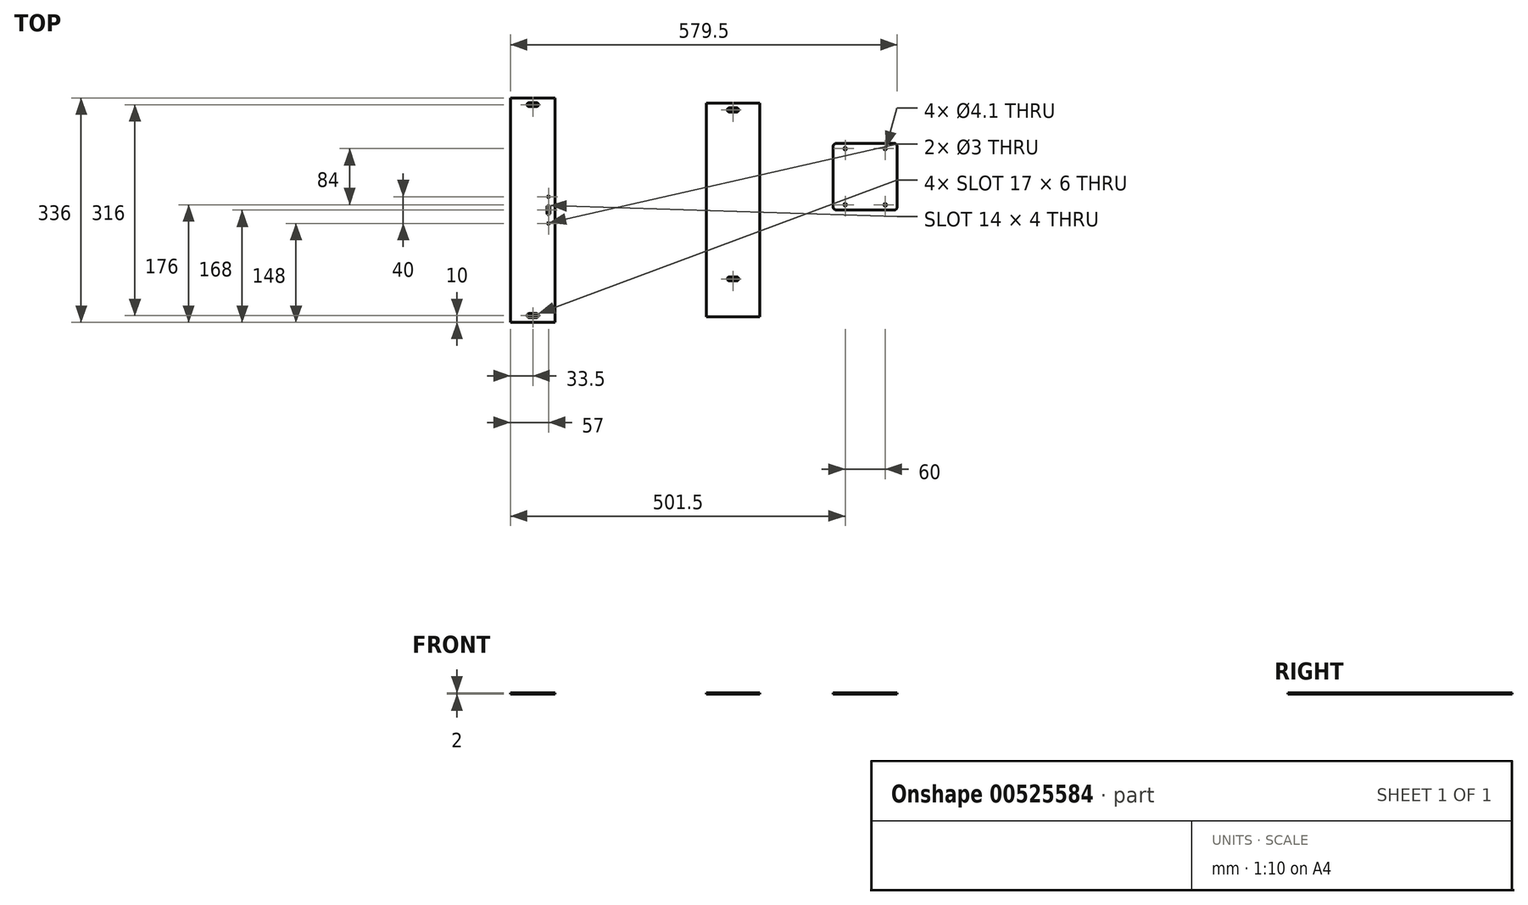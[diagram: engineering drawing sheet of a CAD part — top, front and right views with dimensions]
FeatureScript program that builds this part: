
annotation { "Feature Type Name" : "Feature", "Feature Type Description" : "" }
export const myFeature = defineFeature(function(context is Context, id is Id, definition is map)
    precondition{}
    {
        {
            var Q0;
            Q0=qCreatedBy(makeId("Top.planeOp"),FACE);
            var sketch = newSketch(context, id + "F0", { "sketchPlane" : qUnion([Q0])});
            skLineSegment(sketch, "E0.bottom", {"start": v(40, -160) * mm, "end": v(-40, -160) * mm});
            skLineSegment(sketch, "E0.top", {"start": v(40, 160) * mm, "end": v(-40, 160) * mm});
            skLineSegment(sketch, "E0.left", {"start": v(40, -160) * mm, "end": v(40, 160) * mm});
            skLineSegment(sketch, "E0.right", {"start": v(-40, -160) * mm, "end": v(-40, 160) * mm});
            skPoint(sketch, "E0.middle", {"position": v(0, 0) * mm});
            skLineSegment(sketch, "E1", {"start": v(-186.14, -93) * mm, "end": v(125.12, -93) * mm, "construction": true});
            skLineSegment(sketch, "E2", {"start": v(-183, -113) * mm, "end": v(135.04, -113) * mm, "construction": true});
            skLineSegment(sketch, "E3.bottom", {"start": v(5.5, -106) * mm, "end": v(-5.5, -106) * mm});
            skLineSegment(sketch, "E3.top", {"start": v(5.5, -100) * mm, "end": v(-5.5, -100) * mm});
            skLineSegment(sketch, "E3.left", {"start": v(5.5, -106) * mm, "end": v(5.5, -100) * mm, "construction": true});
            skLineSegment(sketch, "E3.right", {"start": v(-5.5, -106) * mm, "end": v(-5.5, -100) * mm, "construction": true});
            skPoint(sketch, "E3.middle", {"position": v(0, -103) * mm});
            skArc(sketch, "E4", {"start": v(5.5, -106) * mm, "mid": v(8.5, -103) * mm, "end": v(5.5, -100) * mm});
            skArc(sketch, "E5", {"start": v(-5.5, -100) * mm, "mid": v(-8.5, -103) * mm, "end": v(-5.5, -106) * mm});
            skLineSegment(sketch, "E6.bottom", {"start": v(5.5, 147) * mm, "end": v(-5.5, 147) * mm});
            skLineSegment(sketch, "E6.top", {"start": v(5.5, 153) * mm, "end": v(-5.5, 153) * mm});
            skLineSegment(sketch, "E6.left", {"start": v(5.5, 147) * mm, "end": v(5.5, 153) * mm, "construction": true});
            skLineSegment(sketch, "E6.right", {"start": v(-5.5, 147) * mm, "end": v(-5.5, 153) * mm, "construction": true});
            skPoint(sketch, "E6.middle", {"position": v(0, 150) * mm});
            skArc(sketch, "E7", {"start": v(5.5, 147) * mm, "mid": v(8.5, 150) * mm, "end": v(5.5, 153) * mm});
            skArc(sketch, "E8", {"start": v(-5.5, 153) * mm, "mid": v(-8.5, 150) * mm, "end": v(-5.5, 147) * mm});
            skLineSegment(sketch, "E9.bottom", {"start": v(-266.5, -168) * mm, "end": v(-333.5, -168) * mm});
            skLineSegment(sketch, "E9.top", {"start": v(-266.5, 168) * mm, "end": v(-333.5, 168) * mm});
            skLineSegment(sketch, "E9.left", {"start": v(-266.5, -168) * mm, "end": v(-266.5, 168) * mm});
            skLineSegment(sketch, "E9.right", {"start": v(-333.5, -168) * mm, "end": v(-333.5, 168) * mm});
            skPoint(sketch, "E9.middle", {"position": v(-300, 0) * mm});
            skLineSegment(sketch, "E10.bottom", {"start": v(-294.5, 155) * mm, "end": v(-305.5, 155) * mm});
            skLineSegment(sketch, "E10.top", {"start": v(-294.5, 161) * mm, "end": v(-305.5, 161) * mm});
            skLineSegment(sketch, "E10.left", {"start": v(-294.5, 155) * mm, "end": v(-294.5, 161) * mm, "construction": true});
            skLineSegment(sketch, "E10.right", {"start": v(-305.5, 155) * mm, "end": v(-305.5, 161) * mm, "construction": true});
            skPoint(sketch, "E10.middle", {"position": v(-300, 158) * mm});
            skArc(sketch, "E11", {"start": v(-294.5, 155) * mm, "mid": v(-291.5, 158) * mm, "end": v(-294.5, 161) * mm});
            skArc(sketch, "E12", {"start": v(-305.5, 161) * mm, "mid": v(-308.5, 158) * mm, "end": v(-305.5, 155) * mm});
            skLineSegment(sketch, "E13.MirrorCS", {"start": v(-305.5, -155) * mm, "end": v(-305.5, -161) * mm, "construction": true});
            skLineSegment(sketch, "E14.MirrorCS", {"start": v(-294.5, -155) * mm, "end": v(-294.5, -161) * mm, "construction": true});
            skLineSegment(sketch, "E15.MirrorCS", {"start": v(-294.5, -161) * mm, "end": v(-305.5, -161) * mm});
            skArc(sketch, "E16.MirrorCS", {"start": v(-294.5, -155) * mm, "mid": v(-291.5, -158) * mm, "end": v(-294.5, -161) * mm});
            skLineSegment(sketch, "E17.MirrorCS", {"start": v(-294.5, -155) * mm, "end": v(-305.5, -155) * mm});
            skPoint(sketch, "E18.MirrorP", {"position": v(-300, -158) * mm});
            skArc(sketch, "E19.MirrorCS", {"start": v(-305.5, -161) * mm, "mid": v(-308.5, -158) * mm, "end": v(-305.5, -155) * mm});
            skCircle(sketch, "E20", {"center": v(-276.5, 20) * mm, "radius": 1.5 * mm});
            skCircle(sketch, "E21.MirrorC", {"center": v(-276.5, -20) * mm, "radius": 1.5 * mm});
            skLineSegment(sketch, "E22.bottom", {"start": v(-274.5, -5) * mm, "end": v(-278.5, -5) * mm, "construction": true});
            skLineSegment(sketch, "E22.top", {"start": v(-274.5, 5) * mm, "end": v(-278.5, 5) * mm, "construction": true});
            skLineSegment(sketch, "E22.left", {"start": v(-274.5, -5) * mm, "end": v(-274.5, 5) * mm});
            skLineSegment(sketch, "E22.right", {"start": v(-278.5, -5) * mm, "end": v(-278.5, 5) * mm});
            skPoint(sketch, "E22.middle", {"position": v(-276.5, 0) * mm});
            skArc(sketch, "E23", {"start": v(-274.5, 5) * mm, "mid": v(-276.5, 7) * mm, "end": v(-278.5, 5) * mm});
            skArc(sketch, "E24", {"start": v(-278.5, -5) * mm, "mid": v(-276.5, -7) * mm, "end": v(-274.5, -5) * mm});
            skLineSegment(sketch, "E25.bottom", {"start": v(246, 0) * mm, "end": v(150, 0) * mm});
            skLineSegment(sketch, "E25.top", {"start": v(246, 100) * mm, "end": v(150, 100) * mm});
            skLineSegment(sketch, "E25.left", {"start": v(246, 0) * mm, "end": v(246, 100) * mm});
            skLineSegment(sketch, "E25.right", {"start": v(150, 0) * mm, "end": v(150, 100) * mm});
            skPoint(sketch, "E25.middle", {"position": v(198, 50) * mm});
            skCircle(sketch, "E26", {"center": v(168, 92) * mm, "radius": 2.05 * mm});
            skCircle(sketch, "E27", {"center": v(228, 92) * mm, "radius": 2.05 * mm});
            skLineSegment(sketch, "E28", {"start": v(198, 50) * mm, "end": v(329.5, 50) * mm, "construction": true});
            skCircle(sketch, "E29.MirrorC", {"center": v(228, 8) * mm, "radius": 2.05 * mm});
            skCircle(sketch, "E30.MirrorC", {"center": v(168, 8) * mm, "radius": 2.05 * mm});
            skSolve(sketch);
        }
        {
            var Q0;
            Q0 = qSketchRegion(id + "F0", true);
            extrude(context, id + "F1", {"entities" : qUnion([Q0]), "depth" : 2 * mm, "offsetDistance" : 25 * mm});
        }
        {
            var Q0;
            Q0=makeQuery(id+"F1.opExtrude","SWEPT_EDGE",EDGE,{"disambiguationData":[OSD([sQuery(id+"F0.wireOp",EDGE,"E25.bottom"),sQuery(id+"F0.wireOp",EDGE,"E25.right")])]});
            var Q1;
            Q1=makeQuery(id+"F1.opExtrude","SWEPT_EDGE",EDGE,{"disambiguationData":[OSD([sQuery(id+"F0.wireOp",EDGE,"E25.bottom"),sQuery(id+"F0.wireOp",EDGE,"E25.left")])]});
            var Q2;
            Q2=makeQuery(id+"F1.opExtrude","SWEPT_EDGE",EDGE,{"disambiguationData":[OSD([sQuery(id+"F0.wireOp",EDGE,"E25.top"),sQuery(id+"F0.wireOp",EDGE,"E25.left")])]});
            var Q3;
            Q3=makeQuery(id+"F1.opExtrude","SWEPT_EDGE",EDGE,{"disambiguationData":[OSD([sQuery(id+"F0.wireOp",EDGE,"E25.top"),sQuery(id+"F0.wireOp",EDGE,"E25.right")])]});
            fillet(context, id + "F2", {"entities" : qUnion([Q0, Q1, Q2, Q3]), "tangentPropagation" : true, "radius" : 5 * mm, "defaultsChanged" : false, "vertexSettings" : [], "allowEdgeOverflow" : false});
        }
    });
